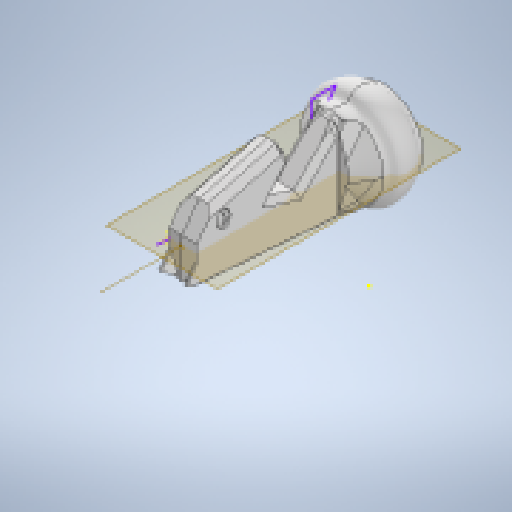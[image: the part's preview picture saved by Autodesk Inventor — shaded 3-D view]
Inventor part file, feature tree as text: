
AUTODESK INVENTOR PART (.ipt)
format: ipt  version: 2024.1 (Build 281209000, 209)  size: 1,059,840 bytes
history: native  units: mm
features: sketch x16, extrude x11, chamfer x10, fillet x10, projected_geometry x6, other x3, mirror x2, sweep x2, revolve x1, plane x1
ambient origin geometry x8: Origin, YZ Plane, XZ Plane, XY Plane, X Axis, Y Axis, Z Axis, Center Point
bodies: Solid1 (feature_tree)
feature tree (62):
  extrude  "Extrusion1"  Depth=3.0mm TaperAngle=0.0deg
  other  "Work Axis1"
  extrude  "Extrusion2"  Depth=14.3mm
  revolve  "Revolution1"  [1 undecoded]
  chamfer  "Chamfer7"  Distance=0.1mm Angle=45.0deg
  extrude  "Extrusion12"  Depth=7.5mm
  extrude  "Extrusion13"  Depth=2.0mm
  extrude  "Extrusion14"  TaperAngle=0.0deg  [1 undecoded]
  fillet  "Fillet9"  Radius=0.679639mm
  fillet  "Fillet10"  Radius=10.0mm
  extrude  "Extrusion15"  Depth=0.5mm
  chamfer  "Chamfer8"  Distance=1.6mm
  sketch  "Sketch23"  dims[d155=5.0mm d156=-1.047198mm d157=0.0mm d158=0.0mm d159=0.679639mm d160=10.0mm d161=-2.443461mm]
  extrude  "Extrusion16"  Depth=1.0mm
  chamfer  "Chamfer9"  Distance=1.0mm
  chamfer  "Chamfer10"  Distance=0.4mm Angle=45.0deg
  extrude  "Extrusion17"  Depth=0.8mm
  fillet  "Fillet11"  Radius=1.3mm
  fillet  "Fillet12"  Radius=1.0mm
  extrude  "Extrusion18"  Depth=0.1mm
  chamfer  "Chamfer11"  [1 undecoded]
  chamfer  "Chamfer12"  Distance=10.0mm
  chamfer  "Chamfer13"  Distance=0.2mm Angle=45.0deg
  extrude  "Extrusion19"  Depth=1.0mm TaperAngle=45.0deg
  chamfer  "Chamfer15"  Distance=0.3mm Angle=45.0deg
  extrude  "Extrusion20"  Depth=1.0mm TaperAngle=0.0deg
  mirror  "Mirror1"
  fillet  "Fillet13"  Radius=1.0mm
  other  "Work Axis14"
  plane  "Work Plane10"
  fillet  "Fillet14"  [1 undecoded]
  sketch  "Sketch35"  dims[d180=1.5mm d181=1.2mm d182=45.0deg d183=0.8mm d184=1.3mm d185=1.0mm d186=0.0mm]
  sweep  "Sweep3"
  sweep  "Sweep4"
  fillet  "Fillet15"  [1 undecoded]
  mirror  "Mirror2"
  chamfer  "Chamfer19"  [1 undecoded]
  fillet  "Fillet16"  Radius=8.0mm
  fillet  "Fillet17"  Radius=8.0mm
  fillet  "Fillet19"  Radius=10.0mm
  chamfer  "Chamfer20"  Distance=1.5mm Angle=45.0deg
  sketch  "Sketch1"  dims[d0=10.0mm d1=3.0mm d2=0.0mm]
  sketch  "Sketch2"  dims[d5=360.0deg d6=14.3mm]
  sketch  "Sketch3"  dims[d7=3.0mm d8=0.0mm d135=0.8mm]
  projected_geometry  "Projected Loop1"
  projected_geometry  "Projected Loop3"
  sketch  "Sketch18"  dims[d146=9.25mm]
  projected_geometry  "Projected Loop4"
  sketch  "Sketch20"  dims[d147=1.0mm d148=0.1mm d149=1.0mm d150=45.0deg]
  projected_geometry  "Projected Loop7"
  sketch  "Sketch21"  dims[d151=36.0mm d152=7.5mm]
  projected_geometry  "Projected Loop8"
  sketch  "Sketch22"  dims[d153=2.5mm d154=2.0mm]
  sketch  "Sketch24"  dims[d162=0.5mm d163=0.5mm]
  sketch  "Sketch25"  dims[d164=3.5mm]
  projected_geometry  "Projected Loop9"
  sketch  "Sketch26"  dims[d165=1.8mm d166=1.6mm d167=0.0mm]
  sketch  "Sketch27"  dims[d168=3.25mm d169=2.0mm d170=45.0deg d171=1.0mm]
  sketch  "Sketch28"  dims[d172=1.4mm d175=1.0mm d176=0.0mm d177=0.4mm d178=2.0mm d179=45.0deg]
  other  "Work Point4"
  sketch  "Sketch36"  dims[d187=0.6mm d188=0.1mm d189=0.0mm d190=0.0mm]
  sketch  "Sketch38"  dims[d191=20.0mm d192=10.0mm d193=0.2mm d194=1.2mm d195=45.0deg d196=1.0mm d197=1.2mm d198=45.0deg d199=0.3mm d200=1.2mm d201=45.0deg d202=1.0mm d203=0.0mm d207=1.0mm d208=1.2mm d209=45.0deg d210=0.0mm d211=0.0mm d212=0.8mm d221=0.5mm d230=0.0mm d231=0.0mm d234=0.0mm d235=0.0mm d236=8.0mm d237=8.0mm d238=10.0mm d239=1.5mm d240=2.0mm d241=45.0deg d242=1.2mm d243=1.2mm d245=2.0mm d246=5.803797mm d247=2.894102mm d248=1.1mm d249=2.0mm d250=45.0deg d98=0.0mm d99=0.0mm d100=0.0mm d101=0.0mm]
note: 6 required parameter values undecoded (feature->parameter linkage not recoverable at this tier; creation-order binding heuristic only, values carry confidence <= 0.55)